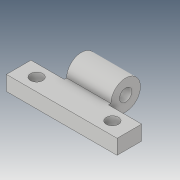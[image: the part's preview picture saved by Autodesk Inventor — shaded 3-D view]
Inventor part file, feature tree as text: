
AUTODESK INVENTOR PART (.ipt)
format: ipt  version: 2019 (Build 230136000, 136)  size: 146,432 bytes
history: native  units: mm
features: extrude x4, sketch x4, move_body x2, fillet x1, plane x1, direct_edit x1
ambient origin geometry x8: Origin, YZ Plane, XZ Plane, XY Plane, X Axis, Y Axis, Z Axis, Center Point
bodies: Solid1 (feature_tree)
feature tree (13):
  extrude  "Extrusion1"  Depth=45.0mm
  sketch  "Sketch4"  dims[d5=5.0mm d6=5.0mm d7=11.0mm]
  extrude  "Extrusion4"  Depth=5.0mm
  fillet  "Fillet1"  Radius=11.0mm
  extrude  "Extrusion5"  Depth=23.0mm
  plane  "Work Plane1"
  extrude  "Extrusion6"  Depth=12.0mm
  direct_edit  "Direct Edit1"
  sketch  "Sketch1"  dims[d0=6.0mm d1=0.0mm d4=45.0mm]
  sketch  "Sketch5"  dims[d8=11.0mm d9=23.0mm]
  sketch  "Sketch6"  dims[d10=10.0mm d20=12.0mm d21=0.0mm d24=3.0mm d25=0.0mm d26=12.0mm d27=5.0mm d28=3.0mm d29=0.0mm d33=5.0mm d34=5.0mm d35=17.8mm d36=7.0mm d37=17.8mm d38=7.1mm d39=30.8mm d40=7.1mm d41=3.0mm d42=0.0mm d46=0.0mm d47=0.0mm d48=-2.5mm d49=0.0mm d50=0.0mm d51=-2.5mm]
  move_body  "Move1"
  move_body  "Move2"
